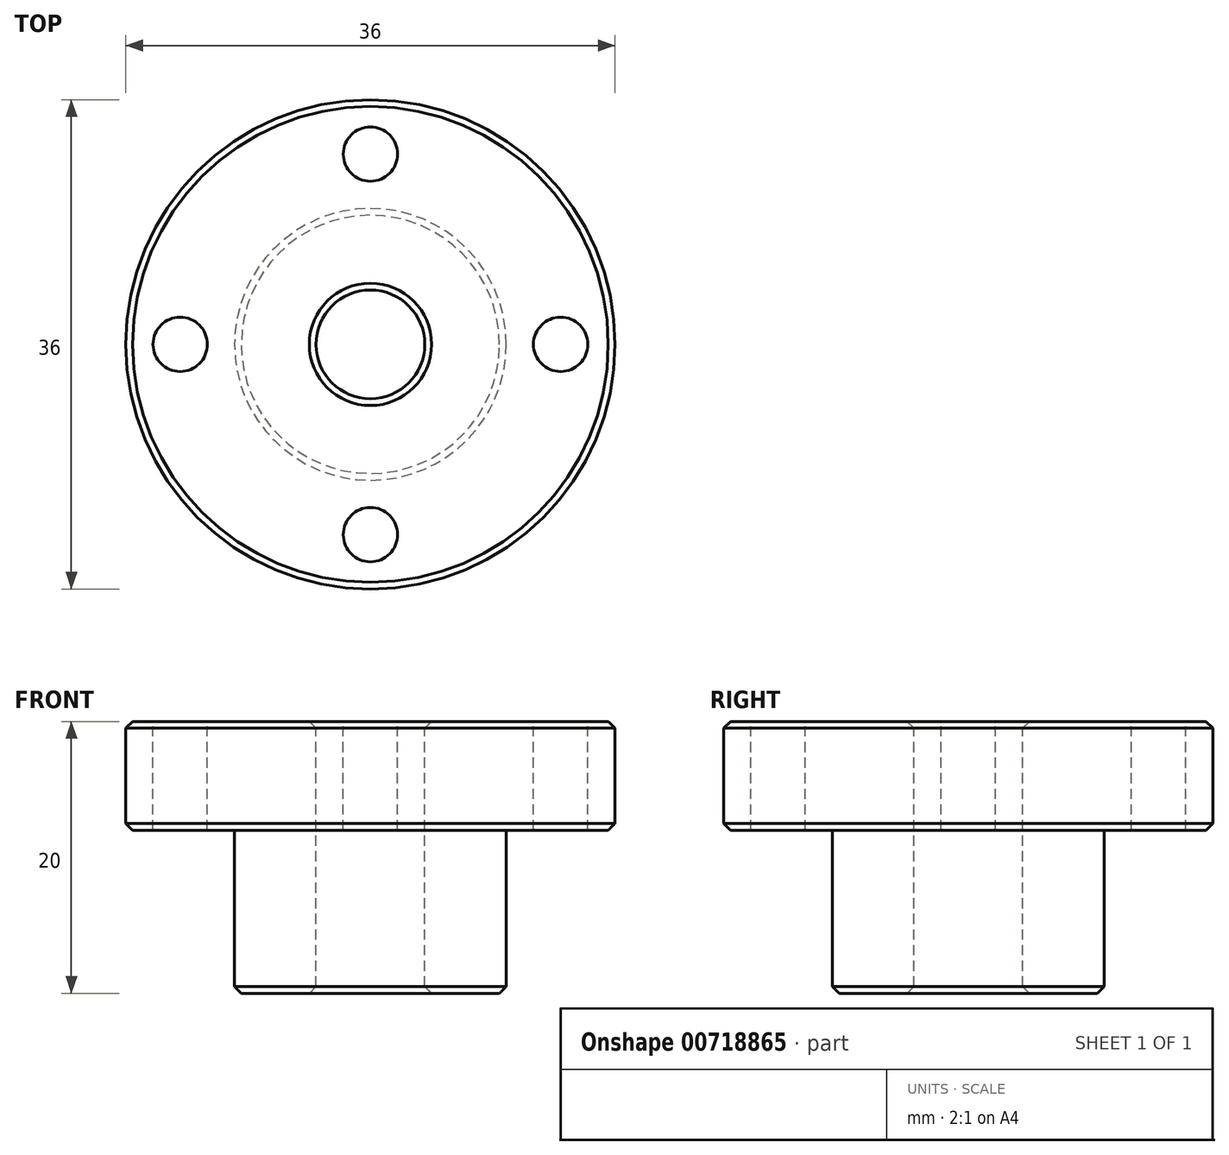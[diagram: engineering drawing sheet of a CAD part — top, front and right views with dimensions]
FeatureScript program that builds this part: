
annotation { "Feature Type Name" : "Feature", "Feature Type Description" : "" }
export const myFeature = defineFeature(function(context is Context, id is Id, definition is map)
    precondition{}
    {
        {
            var Q0;
            Q0=qCreatedBy(makeId("Front.planeOp"),FACE);
            var sketch = newSketch(context, id + "F0", { "sketchPlane" : qUnion([Q0])});
            skLineSegment(sketch, "E0.bottom", {"start": v(4, 0) * mm, "end": v(18, 0) * mm});
            skLineSegment(sketch, "E0.top", {"start": v(10, -8) * mm, "end": v(18, -8) * mm});
            skLineSegment(sketch, "E0.right", {"start": v(18, 0) * mm, "end": v(18, -8) * mm});
            skLineSegment(sketch, "E1.top", {"start": v(4, -20) * mm, "end": v(10, -20) * mm});
            skLineSegment(sketch, "E1.right", {"start": v(10, -8) * mm, "end": v(10, -20) * mm});
            skLineSegment(sketch, "E2", {"start": v(4, 0) * mm, "end": v(4, -20) * mm});
            skLineSegment(sketch, "E3", {"start": v(0, 7) * mm, "end": v(0, -36.65) * mm});
            skSolve(sketch);
        }
        {
            var Q0;
            Q0=makeQuery(id+"F0.imprint","IMPRINT",FACE,{"disambiguationData":[TD([[makeQuery(id+"F0.imprint","IMPRINT",EDGE,{"derivedFrom":sQuery(id+"F0.wireOp",EDGE,"E0.bottom")}),-1.0]])]});
            var Q1;
            Q1=sQuery(id+"F0.wireOp",EDGE,"E3");
            revolve(context, id + "F1", {"surfaceOperationType" : NewSurfaceOperationType.NEW, "entities" : qUnion([Q0]), "axis" : qUnion([Q1]), "revolveType" : RevolveType.FULL});
        }
        {
            var Q0;
            Q0=makeQuery(id+"F1.opRevolve","SWEPT_EDGE",EDGE,{"disambiguationData":[OSD([sQuery(id+"F0.wireOp",EDGE,"E0.bottom"),sQuery(id+"F0.wireOp",EDGE,"E0.right")])]});
            var Q1;
            Q1=makeQuery(id+"F1.opRevolve","SWEPT_EDGE",EDGE,{"disambiguationData":[OSD([sQuery(id+"F0.wireOp",EDGE,"E0.top"),sQuery(id+"F0.wireOp",EDGE,"E0.right")])]});
            var Q2;
            Q2=makeQuery(id+"F1.opRevolve","SWEPT_EDGE",EDGE,{"disambiguationData":[OSD([sQuery(id+"F0.wireOp",EDGE,"E1.top"),sQuery(id+"F0.wireOp",EDGE,"E1.right")])]});
            var Q3;
            Q3=makeQuery(id+"F1.opRevolve","SWEPT_EDGE",EDGE,{"disambiguationData":[OSD([sQuery(id+"F0.wireOp",EDGE,"E0.bottom"),sQuery(id+"F0.wireOp",EDGE,"E2")])]});
            var Q4;
            Q4=makeQuery(id+"F1.opRevolve","SWEPT_EDGE",EDGE,{"disambiguationData":[OSD([sQuery(id+"F0.wireOp",EDGE,"E1.top"),sQuery(id+"F0.wireOp",EDGE,"E2")])]});
            chamfer(context, id + "F2", {"entities" : qUnion([Q0, Q1, Q2, Q3, Q4]), "width" : 0.5 * mm, "tangentPropagation" : true});
        }
        {
            var Q0;
            Q0=makeQuery(id+"F1.opRevolve","SWEPT_FACE",FACE,{"disambiguationData":[OSD([sQuery(id+"F0.wireOp",EDGE,"E0.bottom")])]});
            var sketch = newSketch(context, id + "F3", { "sketchPlane" : qUnion([Q0])});
            skCircle(sketch, "E4", {"center": v(14, 0) * mm, "radius": 2 * mm});
            skCircle(sketch, "E5.MirrorC", {"center": v(-14, 0) * mm, "radius": 2 * mm});
            skCircle(sketch, "E6.1.0", {"center": v(0, 14) * mm, "radius": 2 * mm});
            skCircle(sketch, "E6.3.0", {"center": v(0, -14) * mm, "radius": 2 * mm});
            skPoint(sketch, "E6.center", {"position": v(0, 0) * mm});
            skSolve(sketch);
        }
        {
            var Q0;
            Q0 = qSketchRegion(id + "F3", true);
            extrude(context, id + "F4", {"entities" : qUnion([Q0]), "operationType" : NewBodyOperationType.REMOVE, "oppositeDirection" : true, "depth" : 25 * mm, "offsetDistance" : 25 * mm});
        }
    });
